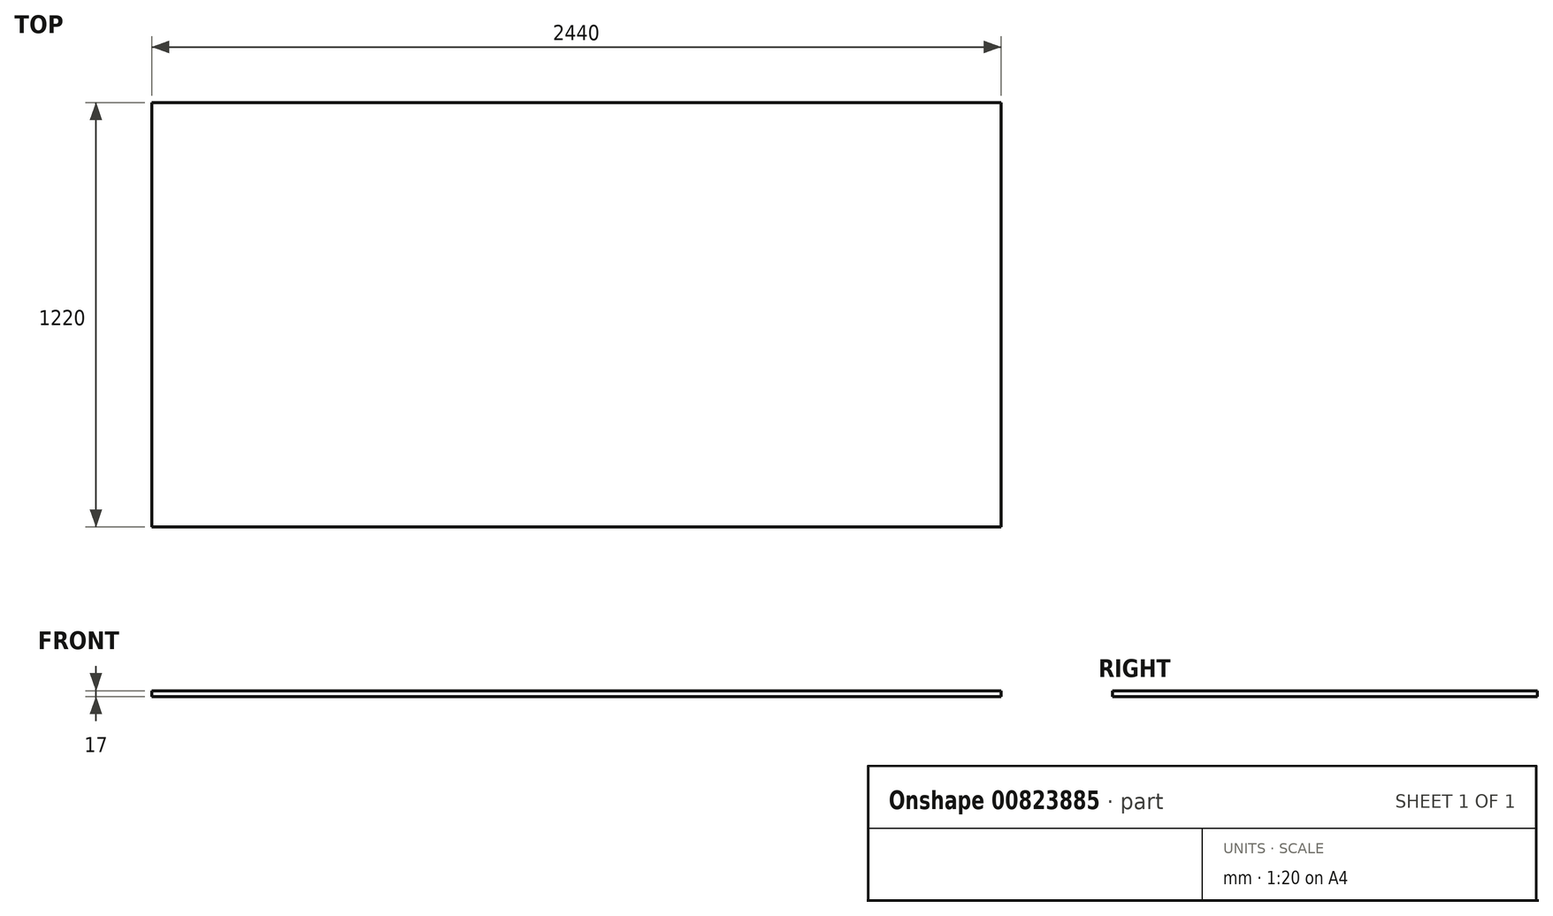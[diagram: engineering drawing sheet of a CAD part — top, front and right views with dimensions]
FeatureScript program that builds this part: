
annotation { "Feature Type Name" : "Feature", "Feature Type Description" : "" }
export const myFeature = defineFeature(function(context is Context, id is Id, definition is map)
    precondition{}
    {
        {
            var Q0;
            Q0=qCreatedBy(makeId("Top.planeOp"),FACE);
            var sketch = newSketch(context, id + "F0", { "sketchPlane" : qUnion([Q0])});
            skLineSegment(sketch, "E0.bottom", {"start": v(-1220, 610) * mm, "end": v(1220, 610) * mm});
            skLineSegment(sketch, "E0.top", {"start": v(-1220, -610) * mm, "end": v(1220, -610) * mm});
            skLineSegment(sketch, "E0.left", {"start": v(-1220, 610) * mm, "end": v(-1220, -610) * mm});
            skLineSegment(sketch, "E0.right", {"start": v(1220, 610) * mm, "end": v(1220, -610) * mm});
            skPoint(sketch, "E0.middle", {"position": v(0, 0) * mm});
            skSolve(sketch);
        }
        {
            var Q0;
            Q0=makeQuery(id+"F0.imprint","IMPRINT",FACE,{"disambiguationData":[TD([[makeQuery(id+"F0.imprint","IMPRINT",EDGE,{"derivedFrom":sQuery(id+"F0.wireOp",EDGE,"E0.bottom")}),-1.0]])]});
            extrude(context, id + "F1", {"entities" : qUnion([Q0]), "depth" : 17 * mm, "offsetDistance" : 25 * mm});
        }
    });
